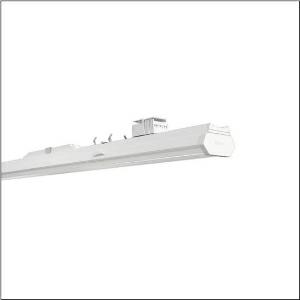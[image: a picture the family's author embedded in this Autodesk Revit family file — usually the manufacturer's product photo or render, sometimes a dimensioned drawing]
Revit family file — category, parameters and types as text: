
# Revit family: licross_r__21_protected_ho_52tp12cn4cxm_7b7d
name_source: partatom
category: Lighting Fixtures
units: mm (PartAtom-declared; Revit-internal decimal feet)

## family parameters
Cut with Voids When Loaded = No
Host = Face
Light Source = No
Part Type = Normal
Room Calculation Point = No
Round Connector Dimension = Use Diameter
Shared = No

## types (1)
- --- (1 x LED, 12460 lm, 68.9 W, 4000K)
    Apparent Load = 69 VA
    CIE Flux Codes = 70 91 97 98 100
    Color Rendering = 80
    Color Temperature = 4000K
    Default Elevation = 1800 mm
    Description = Licross® 21 Protected HO, luminaire insert, of sheet steel, galvanised, coil coated, white, length: 1.500mm, width: 90mm, height: 103mm, LED rated luminous flux: 12.460lm, light colour: 840, control gear: ON/OFF Multilumen, CLOi, control gear: ECG Multilumen, with plug, 3-pole, with phase selection, mains connection: 220..240V, AC, 50/60Hz, start of lifetime: 69W, end of service life: 83W, halogen-free wiring, primary light control with lens, of plastic, primary optical cover: cover, of PMMA, light emission: direct distribution, primary light characteristic: symmetric, protection rating (complete): IP64, insulation class (complete): insulation class I (protective earthing), certification: CE, ENEC, VDE, UKCA, protection symbol: D if used in an environment with conductive dust loads with corresponding accessories, impact resistance: IK06, permissible ambient temperature for indoor applications: -35..+35°C, corresponds to IFS (International Featured Standards) requirements for safety and quality in the food industry, reducing of maximum allowable ambient temperature of 5°C with ceiling mounting, LABS conformity tested according to VDMA 24364:2018-05, packaging unit: 1 piece
    Height = 92 mm
    Lamp = 1 x LED
    Lamp Light Flux = 12460 lm
    Lamp Power = 68.9 W
    Lamp count = 1
    Length = 1500 mm
    Luminous efficacy = 181 lm/W
    Manufacturer = Siteco
    ModVariant = No
    Model = 52TP12CN4CXM
    Mounting Place = Ceiling
    Mounting Type = Pendant
    Number of Poles = 1
    OnlyDefault = Yes
    Power Factor = 1
    Product Name = Licross® 21 Protected HO
    Product group = luminaire insert
    ProductGroupID = 902
    Protection Class = Protection class I
    Protection Degree = IP 64
    RLX_Detail_Level = 1
    RLX_Emergency_Light_Flux = 0 lm
    RLX_Emergency_Type = 0
    RLX_Emergency_Type_DB = No
    RlxData = <blob elided: 22109 chars, md5=00cb18cf>
    Socket = socket
    Standby Power = 0 W
    System Light Flux = 12460 lm
    System Power = 69 W
    Type Comments = factory setting: luminous flux: 100 % | (A | C | E) | 162 mA
    Type Image = l_1256148.jpg
    URL = http://relux.com
    VarID = @adj_111486
    Voltage = 0 V
    Weight = 0.00 kg
    Width = 88 mm

## geometry (parser evidence)
native form markers: Blend x4, Sweep x11
no freeform markers — native parametric forms only
